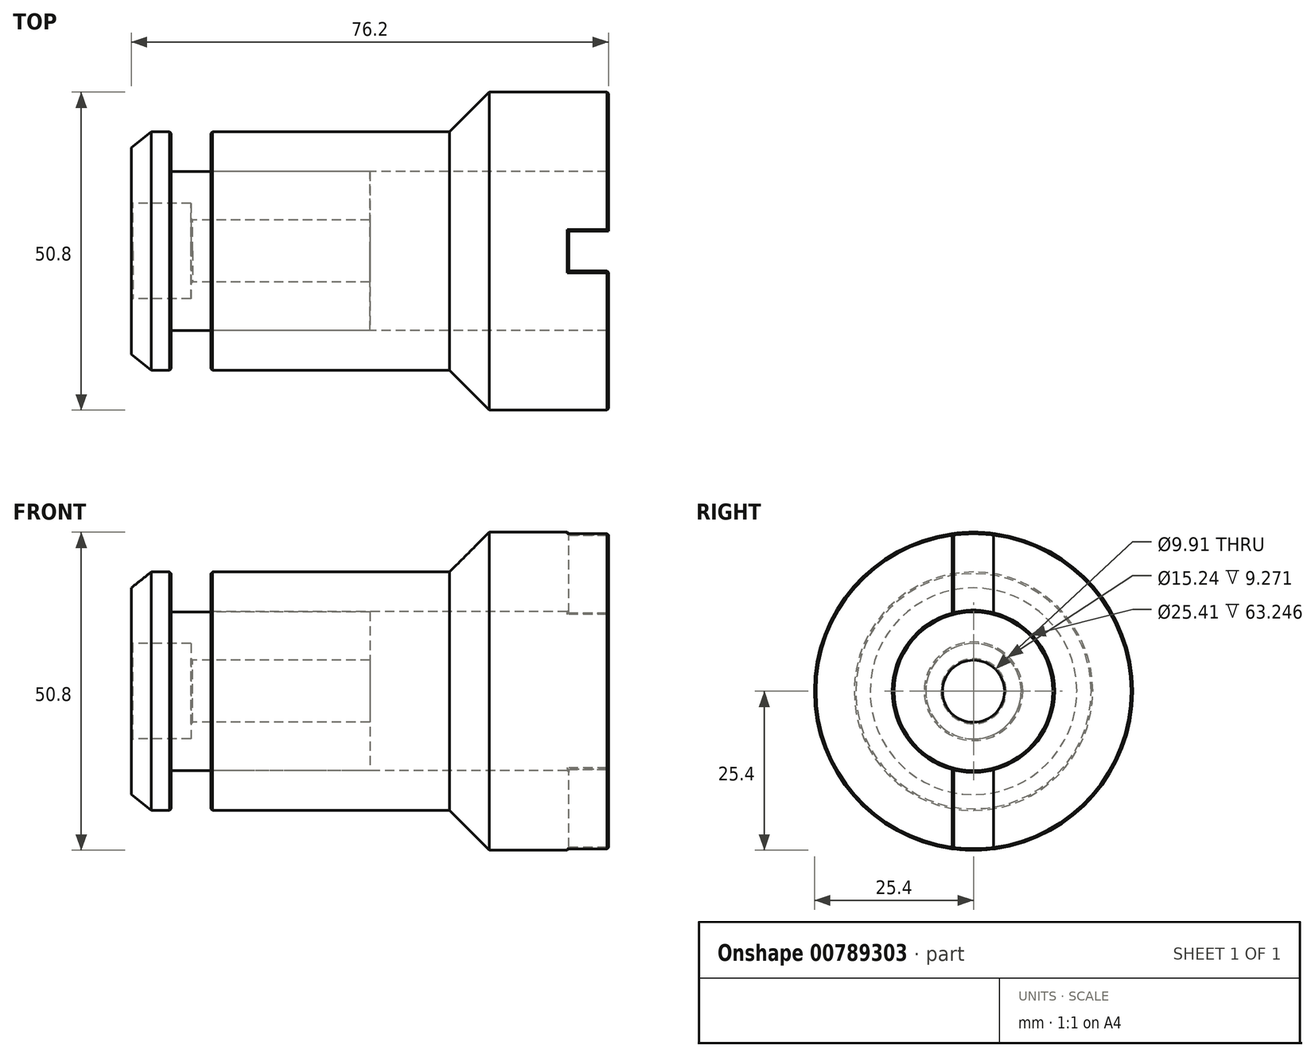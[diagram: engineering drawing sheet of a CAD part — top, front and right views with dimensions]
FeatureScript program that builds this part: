
annotation { "Feature Type Name" : "Feature", "Feature Type Description" : "" }
export const myFeature = defineFeature(function(context is Context, id is Id, definition is map)
    precondition{}
    {
        {
            var Q0;
            Q0=qCreatedBy(makeId("Top.planeOp"),FACE);
            var sketch = newSketch(context, id + "F0", { "sketchPlane" : qUnion([Q0])});
            skLineSegment(sketch, "E0", {"start": v(-98.42, 0) * mm, "end": v(102.72, 0) * mm, "construction": true});
            skLineSegment(sketch, "E1", {"start": v(0, 12.7) * mm, "end": v(-63.5, 12.7) * mm});
            skLineSegment(sketch, "E2", {"start": v(-63.5, 19.05) * mm, "end": v(-25.4, 19.05) * mm});
            skLineSegment(sketch, "E3", {"start": v(-25.4, 19.05) * mm, "end": v(-19.05, 25.4) * mm});
            skLineSegment(sketch, "E4", {"start": v(-19.05, 25.4) * mm, "end": v(0, 25.4) * mm});
            skLineSegment(sketch, "E5", {"start": v(0, 25.4) * mm, "end": v(0, 12.7) * mm});
            skLineSegment(sketch, "E6", {"start": v(-63.5, 12.7) * mm, "end": v(-63.5, 19.05) * mm});
            skSolve(sketch);
        }
        {
            var Q0;
            Q0 = qSketchRegion(id + "F0", true);
            var Q1;
            Q1=sQuery(id+"F0.wireOp",EDGE,"E0");
            revolve(context, id + "F1", {"surfaceOperationType" : NewSurfaceOperationType.NEW, "entities" : qUnion([Q0]), "axis" : qUnion([Q1]), "revolveType" : RevolveType.FULL});
        }
        {
            var Q0;
            Q0=qCreatedBy(makeId("Top.planeOp"),FACE);
            var sketch = newSketch(context, id + "F2", { "sketchPlane" : qUnion([Q0])});
            skLineSegment(sketch, "E7", {"start": v(-38.1, 4.95) * mm, "end": v(-38.1, 12.69) * mm});
            skLineSegment(sketch, "E8", {"start": v(-38.1, 12.69) * mm, "end": v(-69.85, 12.69) * mm});
            skLineSegment(sketch, "E9", {"start": v(-69.85, 12.69) * mm, "end": v(-69.85, 19.05) * mm});
            skLineSegment(sketch, "E10", {"start": v(-69.85, 19.05) * mm, "end": v(-73.02, 19.05) * mm});
            skLineSegment(sketch, "E11", {"start": v(-73.02, 19.05) * mm, "end": v(-76.2, 16.51) * mm});
            skLineSegment(sketch, "E12", {"start": v(-76.2, 16.51) * mm, "end": v(-76.2, 7.62) * mm});
            skLineSegment(sketch, "E13", {"start": v(-66.67, 4.95) * mm, "end": v(-38.1, 4.95) * mm});
            skLineSegment(sketch, "E14", {"start": v(-76.2, 7.62) * mm, "end": v(-66.67, 7.62) * mm});
            skLineSegment(sketch, "E15", {"start": v(-66.67, 7.62) * mm, "end": v(-66.67, 4.95) * mm});
            skPoint(sketch, "E16.orphan", {"position": v(-76.2, 4.95) * mm});
            skSolve(sketch);
        }
        {
            var Q0;
            Q0 = qSketchRegion(id + "F2", true);
            var Q1;
            Q1=sQuery(id+"F0.wireOp",EDGE,"E0");
            revolve(context, id + "F3", {"surfaceOperationType" : NewSurfaceOperationType.NEW, "entities" : qUnion([Q0]), "axis" : qUnion([Q1]), "revolveType" : RevolveType.FULL});
        }
        {
            var Q0;
            Q0=qCreatedBy(makeId("Top.planeOp"),FACE);
            var sketch = newSketch(context, id + "F4", { "sketchPlane" : qUnion([Q0])});
            skLineSegment(sketch, "E17.bottom", {"start": v(0, 3.17) * mm, "end": v(-6.35, 3.17) * mm});
            skLineSegment(sketch, "E17.top", {"start": v(0, -3.17) * mm, "end": v(-6.35, -3.17) * mm});
            skLineSegment(sketch, "E17.left", {"start": v(0, 3.17) * mm, "end": v(0, -3.17) * mm});
            skLineSegment(sketch, "E17.right", {"start": v(-6.35, 3.17) * mm, "end": v(-6.35, -3.17) * mm});
            skSolve(sketch);
        }
        {
            var Q0;
            Q0 = qSketchRegion(id + "F4", true);
            extrude(context, id + "F5", {"entities" : qUnion([Q0]), "operationType" : NewBodyOperationType.REMOVE, "endBound" : BoundingType.SYMMETRIC, "oppositeDirection" : true, "depth" : 76.2 * mm, "offsetDistance" : 25.4 * mm});
        }
        {
            var Q0;
            Q0=makeQuery(id+"F3.opRevolve","SWEPT_EDGE",EDGE,{"disambiguationData":[OSD([sQuery(id+"F2.wireOp",EDGE,"E13"),sQuery(id+"F2.wireOp",EDGE,"E15")])]});
            var Q1;
            Q1=makeQuery(id+"F3.opRevolve","SWEPT_EDGE",EDGE,{"disambiguationData":[OSD([sQuery(id+"F2.wireOp",EDGE,"E12"),sQuery(id+"F2.wireOp",EDGE,"E14")])]});
            var Q2;
            Q2=makeQuery(id+"F3.opRevolve","SWEPT_EDGE",EDGE,{"disambiguationData":[OSD([sQuery(id+"F2.wireOp",EDGE,"E9"),sQuery(id+"F2.wireOp",EDGE,"E10")])]});
            var Q3;
            Q3=makeQuery(id+"F1.opRevolve","SWEPT_EDGE",EDGE,{"disambiguationData":[OSD([sQuery(id+"F0.wireOp",EDGE,"E2"),sQuery(id+"F0.wireOp",EDGE,"E6")])]});
            var Q4;
            {var subQ0=sQuery(id+"F0.wireOp",EDGE,"E4");var subQ1=sQuery(id+"F0.wireOp",EDGE,"E5");Q4=makeQuery(id+"F5.boolean.opBoolean","SPLIT",EDGE,{"disambiguationData":[TD([makeQuery(id+"F5.opExtrude","SWEPT_FACE",FACE,{"disambiguationData":[OSD([sQuery(id+"F4.wireOp",EDGE,"E17.bottom")])]})])],"derivedFrom":makeQuery(id+"F1.opRevolve","SWEPT_EDGE",EDGE,{"disambiguationData":[OSD([subQ0,subQ1])]})});}
            var Q5;
            {var subQ0=sQuery(id+"F0.wireOp",EDGE,"E4");var subQ1=sQuery(id+"F0.wireOp",EDGE,"E5");Q5=makeQuery(id+"F5.boolean.opBoolean","SPLIT",EDGE,{"disambiguationData":[TD([makeQuery(id+"F5.opExtrude","SWEPT_FACE",FACE,{"disambiguationData":[OSD([sQuery(id+"F4.wireOp",EDGE,"E17.top")])]})])],"derivedFrom":makeQuery(id+"F1.opRevolve","SWEPT_EDGE",EDGE,{"disambiguationData":[OSD([subQ0,subQ1])]})});}
            var Q6;
            {var subQ0=sQuery(id+"F0.wireOp",EDGE,"E1");var subQ1=sQuery(id+"F0.wireOp",EDGE,"E5");Q6=makeQuery(id+"F5.boolean.opBoolean","SPLIT",EDGE,{"disambiguationData":[TD([makeQuery(id+"F5.opExtrude","SWEPT_FACE",FACE,{"disambiguationData":[OSD([sQuery(id+"F4.wireOp",EDGE,"E17.top")])]})])],"derivedFrom":makeQuery(id+"F1.opRevolve","SWEPT_EDGE",EDGE,{"disambiguationData":[OSD([subQ0,subQ1])]})});}
            var Q7;
            {var subQ0=sQuery(id+"F0.wireOp",EDGE,"E1");var subQ1=sQuery(id+"F0.wireOp",EDGE,"E5");Q7=makeQuery(id+"F5.boolean.opBoolean","SPLIT",EDGE,{"disambiguationData":[TD([makeQuery(id+"F5.opExtrude","SWEPT_FACE",FACE,{"disambiguationData":[OSD([sQuery(id+"F4.wireOp",EDGE,"E17.bottom")])]})])],"derivedFrom":makeQuery(id+"F1.opRevolve","SWEPT_EDGE",EDGE,{"disambiguationData":[OSD([subQ0,subQ1])]})});}
            var Q8;
            Q8=makeQuery(id+"F5.boolean.opBoolean","COPY",EDGE,{"disambiguationData":[OD(0.0)],"derivedFrom":makeQuery(id+"F5.opExtrude","SWEPT_EDGE",EDGE,{"disambiguationData":[OSD([sQuery(id+"F4.wireOp",EDGE,"E17.bottom"),sQuery(id+"F4.wireOp",EDGE,"E17.left")])]})});
            var Q9;
            Q9=makeQuery(id+"F5.boolean.opBoolean","COPY",EDGE,{"disambiguationData":[OD(0.0)],"derivedFrom":makeQuery(id+"F5.opExtrude","SWEPT_EDGE",EDGE,{"disambiguationData":[OSD([sQuery(id+"F4.wireOp",EDGE,"E17.top"),sQuery(id+"F4.wireOp",EDGE,"E17.left")])]})});
            var Q10;
            Q10=makeQuery(id+"F5.boolean.opBoolean","COPY",EDGE,{"disambiguationData":[OD(1.0)],"derivedFrom":makeQuery(id+"F5.opExtrude","SWEPT_EDGE",EDGE,{"disambiguationData":[OSD([sQuery(id+"F4.wireOp",EDGE,"E17.top"),sQuery(id+"F4.wireOp",EDGE,"E17.left")])]})});
            var Q11;
            Q11=makeQuery(id+"F5.boolean.opBoolean","COPY",EDGE,{"disambiguationData":[OD(1.0)],"derivedFrom":makeQuery(id+"F5.opExtrude","SWEPT_EDGE",EDGE,{"disambiguationData":[OSD([sQuery(id+"F4.wireOp",EDGE,"E17.bottom"),sQuery(id+"F4.wireOp",EDGE,"E17.left")])]})});
            var Q12;
            Q12=makeQuery(id+"F5.boolean.opBoolean","INTERSECT",EDGE,{"disambiguationData":[OD(1.0)],"derivedFrom":[makeQuery(id+"F1.opRevolve","SWEPT_FACE",FACE,{"disambiguationData":[OSD([sQuery(id+"F0.wireOp",EDGE,"E4")])]}),makeQuery(id+"F5.opExtrude","SWEPT_FACE",FACE,{"disambiguationData":[OSD([sQuery(id+"F4.wireOp",EDGE,"E17.top")])]})]});
            var Q13;
            Q13=makeQuery(id+"F5.boolean.opBoolean","INTERSECT",EDGE,{"disambiguationData":[OD(1.0)],"derivedFrom":[makeQuery(id+"F1.opRevolve","SWEPT_FACE",FACE,{"disambiguationData":[OSD([sQuery(id+"F0.wireOp",EDGE,"E4")])]}),makeQuery(id+"F5.opExtrude","SWEPT_FACE",FACE,{"disambiguationData":[OSD([sQuery(id+"F4.wireOp",EDGE,"E17.right")])]})]});
            var Q14;
            Q14=makeQuery(id+"F5.boolean.opBoolean","INTERSECT",EDGE,{"disambiguationData":[OD(1.0)],"derivedFrom":[makeQuery(id+"F1.opRevolve","SWEPT_FACE",FACE,{"disambiguationData":[OSD([sQuery(id+"F0.wireOp",EDGE,"E4")])]}),makeQuery(id+"F5.opExtrude","SWEPT_FACE",FACE,{"disambiguationData":[OSD([sQuery(id+"F4.wireOp",EDGE,"E17.bottom")])]})]});
            var Q15;
            Q15=makeQuery(id+"F5.boolean.opBoolean","INTERSECT",EDGE,{"disambiguationData":[OD(1.0)],"derivedFrom":[makeQuery(id+"F1.opRevolve","SWEPT_FACE",FACE,{"disambiguationData":[OSD([sQuery(id+"F0.wireOp",EDGE,"E1")])]}),makeQuery(id+"F5.opExtrude","SWEPT_FACE",FACE,{"disambiguationData":[OSD([sQuery(id+"F4.wireOp",EDGE,"E17.top")])]})]});
            var Q16;
            Q16=makeQuery(id+"F5.boolean.opBoolean","INTERSECT",EDGE,{"disambiguationData":[OD(1.0)],"derivedFrom":[makeQuery(id+"F1.opRevolve","SWEPT_FACE",FACE,{"disambiguationData":[OSD([sQuery(id+"F0.wireOp",EDGE,"E1")])]}),makeQuery(id+"F5.opExtrude","SWEPT_FACE",FACE,{"disambiguationData":[OSD([sQuery(id+"F4.wireOp",EDGE,"E17.right")])]})]});
            var Q17;
            Q17=makeQuery(id+"F5.boolean.opBoolean","INTERSECT",EDGE,{"disambiguationData":[OD(1.0)],"derivedFrom":[makeQuery(id+"F1.opRevolve","SWEPT_FACE",FACE,{"disambiguationData":[OSD([sQuery(id+"F0.wireOp",EDGE,"E1")])]}),makeQuery(id+"F5.opExtrude","SWEPT_FACE",FACE,{"disambiguationData":[OSD([sQuery(id+"F4.wireOp",EDGE,"E17.bottom")])]})]});
            var Q18;
            Q18=makeQuery(id+"F5.boolean.opBoolean","INTERSECT",EDGE,{"disambiguationData":[OD(0.0)],"derivedFrom":[makeQuery(id+"F1.opRevolve","SWEPT_FACE",FACE,{"disambiguationData":[OSD([sQuery(id+"F0.wireOp",EDGE,"E4")])]}),makeQuery(id+"F5.opExtrude","SWEPT_FACE",FACE,{"disambiguationData":[OSD([sQuery(id+"F4.wireOp",EDGE,"E17.top")])]})]});
            var Q19;
            Q19=makeQuery(id+"F5.boolean.opBoolean","INTERSECT",EDGE,{"disambiguationData":[OD(0.0)],"derivedFrom":[makeQuery(id+"F1.opRevolve","SWEPT_FACE",FACE,{"disambiguationData":[OSD([sQuery(id+"F0.wireOp",EDGE,"E4")])]}),makeQuery(id+"F5.opExtrude","SWEPT_FACE",FACE,{"disambiguationData":[OSD([sQuery(id+"F4.wireOp",EDGE,"E17.right")])]})]});
            var Q20;
            Q20=makeQuery(id+"F5.boolean.opBoolean","INTERSECT",EDGE,{"disambiguationData":[OD(0.0)],"derivedFrom":[makeQuery(id+"F1.opRevolve","SWEPT_FACE",FACE,{"disambiguationData":[OSD([sQuery(id+"F0.wireOp",EDGE,"E4")])]}),makeQuery(id+"F5.opExtrude","SWEPT_FACE",FACE,{"disambiguationData":[OSD([sQuery(id+"F4.wireOp",EDGE,"E17.bottom")])]})]});
            var Q21;
            Q21=makeQuery(id+"F5.boolean.opBoolean","INTERSECT",EDGE,{"disambiguationData":[OD(0.0)],"derivedFrom":[makeQuery(id+"F1.opRevolve","SWEPT_FACE",FACE,{"disambiguationData":[OSD([sQuery(id+"F0.wireOp",EDGE,"E1")])]}),makeQuery(id+"F5.opExtrude","SWEPT_FACE",FACE,{"disambiguationData":[OSD([sQuery(id+"F4.wireOp",EDGE,"E17.top")])]})]});
            var Q22;
            Q22=makeQuery(id+"F5.boolean.opBoolean","INTERSECT",EDGE,{"disambiguationData":[OD(0.0)],"derivedFrom":[makeQuery(id+"F1.opRevolve","SWEPT_FACE",FACE,{"disambiguationData":[OSD([sQuery(id+"F0.wireOp",EDGE,"E1")])]}),makeQuery(id+"F5.opExtrude","SWEPT_FACE",FACE,{"disambiguationData":[OSD([sQuery(id+"F4.wireOp",EDGE,"E17.right")])]})]});
            var Q23;
            Q23=makeQuery(id+"F5.boolean.opBoolean","INTERSECT",EDGE,{"disambiguationData":[OD(0.0)],"derivedFrom":[makeQuery(id+"F1.opRevolve","SWEPT_FACE",FACE,{"disambiguationData":[OSD([sQuery(id+"F0.wireOp",EDGE,"E1")])]}),makeQuery(id+"F5.opExtrude","SWEPT_FACE",FACE,{"disambiguationData":[OSD([sQuery(id+"F4.wireOp",EDGE,"E17.bottom")])]})]});
            chamfer(context, id + "F6", {"entities" : qUnion([Q0, Q1, Q2, Q3, Q4, Q5, Q6, Q7, Q8, Q9, Q10, Q11, Q12, Q13, Q14, Q15, Q16, Q17, Q18, Q19, Q20, Q21, Q22, Q23]), "width" : 0.25 * mm, "tangentPropagation" : true});
        }
    });
